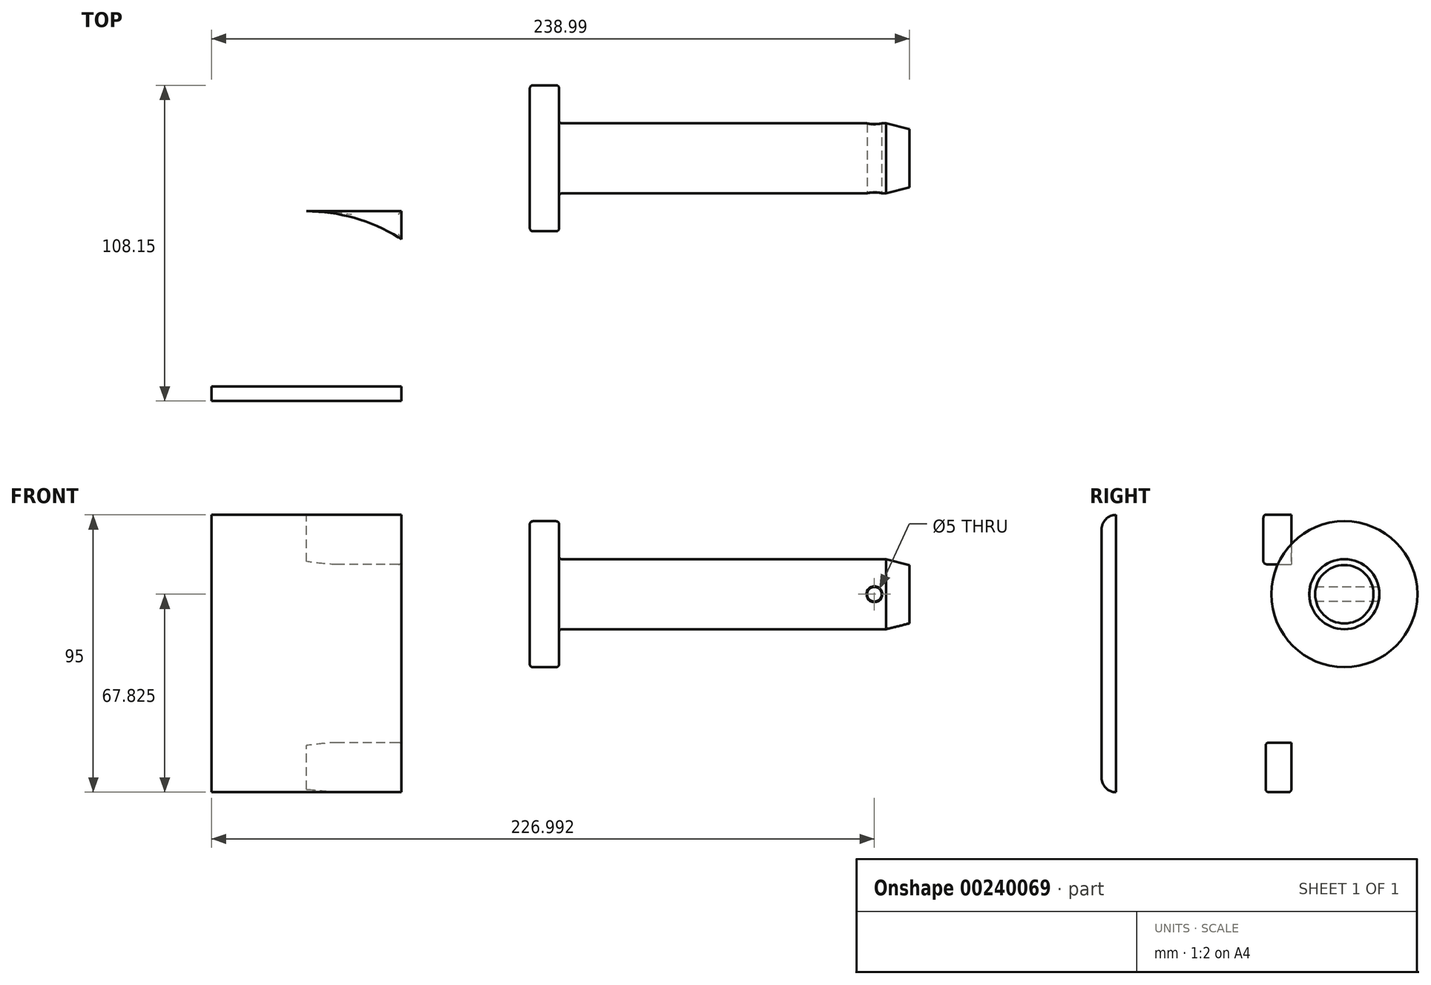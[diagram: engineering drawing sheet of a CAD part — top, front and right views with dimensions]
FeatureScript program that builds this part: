
annotation { "Feature Type Name" : "Feature", "Feature Type Description" : "" }
export const myFeature = defineFeature(function(context is Context, id is Id, definition is map)
    precondition{}
    {
        {
            var Q0;
            Q0=qCreatedBy(makeId("Right.planeOp"),FACE);
            var sketch = newSketch(context, id + "F0", { "sketchPlane" : qUnion([Q0])});
            skLineSegment(sketch, "E0", {"start": v(-83.15, 71.47) * mm, "end": v(-83.15, -13.53) * mm});
            skLineSegment(sketch, "E1", {"start": v(-78.15, 76.47) * mm, "end": v(-18.15, 76.47) * mm});
            skLineSegment(sketch, "E2", {"start": v(-78.15, -18.53) * mm, "end": v(-18.15, -18.53) * mm});
            skPoint(sketch, "E3.visualSharp", {"position": v(-83.15, 76.47) * mm});
            skArc(sketch, "E3.filletArc", {"start": v(-78.15, 76.47) * mm, "mid": v(-81.68, 75) * mm, "end": v(-83.15, 71.47) * mm});
            skPoint(sketch, "E4.visualSharp", {"position": v(-83.15, -18.53) * mm});
            skArc(sketch, "E4.filletArc", {"start": v(-83.15, -13.53) * mm, "mid": v(-81.68, -17.07) * mm, "end": v(-78.15, -18.53) * mm});
            skLineSegment(sketch, "E5.0", {"start": v(-65.15, 59.47) * mm, "end": v(-18.15, 59.47) * mm});
            skLineSegment(sketch, "E5.1", {"start": v(-66.15, 58.47) * mm, "end": v(-66.15, -0.53) * mm});
            skLineSegment(sketch, "E5.2", {"start": v(-65.15, -1.53) * mm, "end": v(-18.15, -1.53) * mm});
            skLineSegment(sketch, "E6", {"start": v(-18.15, 76.47) * mm, "end": v(-18.15, 59.47) * mm});
            skLineSegment(sketch, "E7", {"start": v(-18.15, -1.53) * mm, "end": v(-18.15, -18.53) * mm});
            skPoint(sketch, "E8.visualSharp", {"position": v(-66.15, 59.47) * mm});
            skArc(sketch, "E8.filletArc", {"start": v(-65.15, 59.47) * mm, "mid": v(-65.86, 59.17) * mm, "end": v(-66.15, 58.47) * mm});
            skPoint(sketch, "E9.visualSharp", {"position": v(-66.15, -1.53) * mm});
            skArc(sketch, "E9.filletArc", {"start": v(-66.15, -0.53) * mm, "mid": v(-65.86, -1.24) * mm, "end": v(-65.15, -1.53) * mm});
            skSolve(sketch);
        }
        {
            var Q0;
            Q0=makeQuery(id+"F0.imprint","IMPRINT",FACE,{"disambiguationData":[TD([[makeQuery(id+"F0.imprint","IMPRINT",EDGE,{"derivedFrom":sQuery(id+"F0.wireOp",EDGE,"E0")}),1.0]])]});
            extrude(context, id + "F1", {"entities" : qUnion([Q0]), "depth" : 65 * mm});
        }
        {
            var Q0;
            Q0=makeQuery(id+"F1.opExtrude","SWEPT_FACE",FACE,{"disambiguationData":[OSD([sQuery(id+"F0.wireOp",EDGE,"E1")])]});
            var sketch = newSketch(context, id + "F2", { "sketchPlane" : qUnion([Q0])});
            skCircle(sketch, "E10", {"center": v(32.5, -43.65) * mm, "radius": 12.5 * mm});
            skPoint(sketch, "E11", {"position": v(32.5, -18.15) * mm});
            skArc(sketch, "E12", {"start": v(32.5, -18.15) * mm, "mid": v(49.44, -20.59) * mm, "end": v(65, -27.71) * mm});
            skArc(sketch, "E13", {"start": v(32.5, -18.15) * mm, "mid": v(15.56, -20.59) * mm, "end": v(0, -27.71) * mm});
            skSolve(sketch);
        }
        {
            var Q0;
            Q0=makeQuery(id+"F2.imprint","IMPRINT",FACE,{"disambiguationData":[TD([[makeQuery(id+"F2.imprint","IMPRINT",EDGE,{"derivedFrom":sQuery(id+"F2.wireOp",EDGE,"E10")}),1.0]])]});
            extrude(context, id + "F3", {"entities" : qUnion([Q0]), "operationType" : NewBodyOperationType.REMOVE, "endBound" : BoundingType.THROUGH_ALL, "oppositeDirection" : true, "depth" : 25 * mm});
        }
        {
            var Q0;
            {var subQ0=sQuery(id+"F2.wireOp",EDGE,"E13");Q0=makeQuery(id+"F2.imprint","IMPRINT",FACE,{"disambiguationData":[TD([[makeQuery(id+"F2.imprint","IMPRINT",EDGE,{"derivedFrom":subQ0}),-1.0]])]});}
            extrude(context, id + "F4", {"entities" : qUnion([Q0]), "operationType" : NewBodyOperationType.REMOVE, "endBound" : BoundingType.THROUGH_ALL, "oppositeDirection" : true, "depth" : 25 * mm});
        }
        {
            var Q0;
            {var subQ0=sQuery(id+"F2.wireOp",EDGE,"E12");Q0=makeQuery(id+"F2.imprint","IMPRINT",FACE,{"disambiguationData":[TD([[makeQuery(id+"F2.imprint","IMPRINT",EDGE,{"derivedFrom":subQ0}),1.0]])]});}
            extrude(context, id + "F5", {"entities" : qUnion([Q0]), "operationType" : NewBodyOperationType.REMOVE, "endBound" : BoundingType.THROUGH_ALL, "oppositeDirection" : true, "depth" : 25 * mm});
        }
        {
            var Q0;
            Q0=qCreatedBy(makeId("Front.planeOp"),FACE);
            var sketch = newSketch(context, id + "F6", { "sketchPlane" : qUnion([Q0])});
            skLineSegment(sketch, "E14", {"start": v(239, 49.3) * mm, "end": v(109, 49.3) * mm});
            skLineSegment(sketch, "E15", {"start": v(239, 49.3) * mm, "end": v(239, 59.3) * mm});
            skLineSegment(sketch, "E16", {"start": v(109, 49.3) * mm, "end": v(109, 73.3) * mm});
            skLineSegment(sketch, "E17", {"start": v(110, 74.3) * mm, "end": v(118, 74.3) * mm});
            skLineSegment(sketch, "E18", {"start": v(119, 73.3) * mm, "end": v(119, 62.3) * mm});
            skLineSegment(sketch, "E19", {"start": v(120, 61.3) * mm, "end": v(231, 61.3) * mm});
            skLineSegment(sketch, "E20", {"start": v(239, 59.3) * mm, "end": v(231, 61.3) * mm});
            skPoint(sketch, "E21.orphan", {"position": v(239, 61.3) * mm});
            skPoint(sketch, "E22.visualSharp", {"position": v(119, 61.3) * mm});
            skArc(sketch, "E22.filletArc", {"start": v(119, 62.3) * mm, "mid": v(119.29, 61.59) * mm, "end": v(120, 61.3) * mm});
            skPoint(sketch, "E23.visualSharp", {"position": v(119, 74.3) * mm});
            skArc(sketch, "E23.filletArc", {"start": v(119, 73.3) * mm, "mid": v(118.7, 74) * mm, "end": v(118, 74.3) * mm});
            skPoint(sketch, "E24.visualSharp", {"position": v(109, 74.3) * mm});
            skArc(sketch, "E24.filletArc", {"start": v(110, 74.3) * mm, "mid": v(109.29, 74) * mm, "end": v(109, 73.3) * mm});
            skSolve(sketch);
        }
        {
            var Q0;
            Q0=makeQuery(id+"F6.imprint","IMPRINT",FACE,{"disambiguationData":[TD([[makeQuery(id+"F6.imprint","IMPRINT",EDGE,{"derivedFrom":sQuery(id+"F6.wireOp",EDGE,"E14")}),-1.0]])]});
            var Q1;
            Q1=sQuery(id+"F6.wireOp",EDGE,"E14");
            revolve(context, id + "F7", {"entities" : qUnion([Q0]), "axis" : qUnion([Q1]), "revolveType" : RevolveType.FULL});
        }
        {
            var Q0;
            Q0=qCreatedBy(makeId("Front.planeOp"),FACE);
            var sketch = newSketch(context, id + "F8", { "sketchPlane" : qUnion([Q0])});
            skCircle(sketch, "E25", {"center": v(227, 49.3) * mm, "radius": 2.5 * mm});
            skSolve(sketch);
        }
        {
            var Q0;
            Q0 = qSketchRegion(id + "F8", true);
            extrude(context, id + "F9", {"entities" : qUnion([Q0]), "operationType" : NewBodyOperationType.REMOVE, "endBound" : BoundingType.SYMMETRIC, "oppositeDirection" : true, "depth" : 50 * mm});
        }
        {
            var Q0;
            Q0=makeQuery(id+"F9.boolean.opBoolean","INTERSECT",EDGE,{"disambiguationData":[OD(1.0)],"derivedFrom":[makeQuery(id+"F7.opRevolve","SWEPT_FACE",FACE,{"disambiguationData":[OSD([sQuery(id+"F6.wireOp",EDGE,"E19")])]}),makeQuery(id+"F9.opExtrude","SWEPT_FACE",FACE,{"disambiguationData":[OSD([sQuery(id+"F8.wireOp",EDGE,"E25")])]})]});
            fillet(context, id + "F10", {"entities" : qUnion([Q0]), "radius" : .2 * mm, "tangentPropagation" : true, "allowEdgeOverflow" : false});
        }
        {
            var Q0;
            Q0=makeQuery(id+"F9.boolean.opBoolean","INTERSECT",EDGE,{"disambiguationData":[OD(0.0)],"derivedFrom":[makeQuery(id+"F7.opRevolve","SWEPT_FACE",FACE,{"disambiguationData":[OSD([sQuery(id+"F6.wireOp",EDGE,"E19")])]}),makeQuery(id+"F9.opExtrude","SWEPT_FACE",FACE,{"disambiguationData":[OSD([sQuery(id+"F8.wireOp",EDGE,"E25")])]})]});
            fillet(context, id + "F11", {"entities" : qUnion([Q0]), "radius" : .2 * mm, "tangentPropagation" : true, "allowEdgeOverflow" : false});
        }
        {
            var Q0;
            Q0=makeQuery(id+"F1.opExtrude","CAP_EDGE",EDGE,{"disambiguationData":[OSD([sQuery(id+"F0.wireOp",EDGE,"E1")])],"isStart":true});
            var Q1;
            Q1=makeQuery(id+"F5.boolean.opBoolean","MERGE",EDGE,{"derivedFrom":[makeQuery(id+"F4.boolean.opBoolean","COPY",EDGE,{"derivedFrom":makeQuery(id+"F4.opExtrude","CAP_EDGE",EDGE,{"disambiguationData":[OSD([sQuery(id+"F2.wireOp",EDGE,"E13")])],"isStart":true})}),makeQuery(id+"F5.opExtrude","CAP_EDGE",EDGE,{"disambiguationData":[OSD([sQuery(id+"F2.wireOp",EDGE,"E12")])],"isStart":true})]});
            var Q2;
            Q2=makeQuery(id+"F5.boolean.opBoolean","INTERSECT",EDGE,{"derivedFrom":[makeQuery(id+"F1.opExtrude","SWEPT_FACE",FACE,{"disambiguationData":[OSD([sQuery(id+"F0.wireOp",EDGE,"E5.0")])]}),makeQuery(id+"F5.opExtrude","SWEPT_FACE",FACE,{"disambiguationData":[OSD([sQuery(id+"F2.wireOp",EDGE,"E12")])]})]});
            var Q3;
            Q3=makeQuery(id+"F1.opExtrude","CAP_EDGE",EDGE,{"disambiguationData":[OSD([sQuery(id+"F0.wireOp",EDGE,"E5.0")])],"isStart":true});
            var Q4;
            Q4=makeQuery(id+"F1.opExtrude","CAP_EDGE",EDGE,{"disambiguationData":[OSD([sQuery(id+"F0.wireOp",EDGE,"E1")])],"isStart":false});
            var Q5;
            Q5=makeQuery(id+"F1.opExtrude","CAP_EDGE",EDGE,{"disambiguationData":[OSD([sQuery(id+"F0.wireOp",EDGE,"E5.2")])],"isStart":false});
            var Q6;
            Q6=makeQuery(id+"F1.opExtrude","CAP_EDGE",EDGE,{"disambiguationData":[OSD([sQuery(id+"F0.wireOp",EDGE,"E5.1")])],"isStart":false});
            var Q7;
            Q7=makeQuery(id+"F5.boolean.opBoolean","INTERSECT",EDGE,{"derivedFrom":[makeQuery(id+"F1.opExtrude","SWEPT_FACE",FACE,{"disambiguationData":[OSD([sQuery(id+"F0.wireOp",EDGE,"E5.2")])]}),makeQuery(id+"F5.opExtrude","SWEPT_FACE",FACE,{"disambiguationData":[OSD([sQuery(id+"F2.wireOp",EDGE,"E12")])]})]});
            var Q8;
            {var subQ9=sQuery(id+"F0.wireOp",EDGE,"E2");var subQ10=sQuery(id+"F0.wireOp",EDGE,"E1");var subQ12=makeQuery(id+"F1.opExtrude","SWEPT_FACE",FACE,{"disambiguationData":[OSD([subQ9])]});var subQ14=sQuery(id+"F2.wireOp",EDGE,"E12");Q8=makeQuery(id+"F5.boolean.opBoolean","COPY",EDGE,{"disambiguationData":[TD([subQ12])],"derivedFrom":makeQuery(id+"F5.opExtrude","SWEPT_EDGE",EDGE,{"disambiguationData":[OSD([subQ10,subQ14])]})});}
            var Q9;
            {var subQ10=sQuery(id+"F0.wireOp",EDGE,"E1");var subQ12=makeQuery(id+"F1.opExtrude","SWEPT_FACE",FACE,{"disambiguationData":[OSD([subQ10])]});var subQ14=sQuery(id+"F2.wireOp",EDGE,"E12");Q9=makeQuery(id+"F5.boolean.opBoolean","COPY",EDGE,{"disambiguationData":[TD([subQ12])],"derivedFrom":makeQuery(id+"F5.opExtrude","SWEPT_EDGE",EDGE,{"disambiguationData":[OSD([subQ10,subQ14])]})});}
            var Q10;
            Q10=makeQuery(id+"F5.boolean.opBoolean","INTERSECT",EDGE,{"derivedFrom":[makeQuery(id+"F1.opExtrude","SWEPT_FACE",FACE,{"disambiguationData":[OSD([sQuery(id+"F0.wireOp",EDGE,"E2")])]}),makeQuery(id+"F5.opExtrude","SWEPT_FACE",FACE,{"disambiguationData":[OSD([sQuery(id+"F2.wireOp",EDGE,"E12")])]})]});
            var Q11;
            {var subQ1=sQuery(id+"F0.wireOp",EDGE,"E2");var subQ2=sQuery(id+"F0.wireOp",EDGE,"E1");var subQ3=sQuery(id+"F2.wireOp",EDGE,"E13");Q11=makeQuery(id+"F4.boolean.opBoolean","COPY",EDGE,{"disambiguationData":[TD([makeQuery(id+"F1.opExtrude","SWEPT_FACE",FACE,{"disambiguationData":[OSD([subQ1])]})])],"derivedFrom":makeQuery(id+"F4.opExtrude","SWEPT_EDGE",EDGE,{"disambiguationData":[OSD([subQ2,subQ3])]})});}
            var Q12;
            {var subQ1=sQuery(id+"F0.wireOp",EDGE,"E1");var subQ2=sQuery(id+"F2.wireOp",EDGE,"E13");Q12=makeQuery(id+"F4.boolean.opBoolean","COPY",EDGE,{"disambiguationData":[TD([makeQuery(id+"F1.opExtrude","SWEPT_FACE",FACE,{"disambiguationData":[OSD([subQ1])]})])],"derivedFrom":makeQuery(id+"F4.opExtrude","SWEPT_EDGE",EDGE,{"disambiguationData":[OSD([subQ1,subQ2])]})});}
            var Q13;
            Q13=makeQuery(id+"F1.opExtrude","CAP_EDGE",EDGE,{"disambiguationData":[OSD([sQuery(id+"F0.wireOp",EDGE,"E5.0")])],"isStart":false});
            var Q14;
            Q14=makeQuery(id+"F1.opExtrude","SWEPT_FACE",FACE,{"disambiguationData":[OSD([sQuery(id+"F0.wireOp",EDGE,"E2")])]});
            var Q15;
            Q15=makeQuery(id+"F1.opExtrude","CAP_EDGE",EDGE,{"disambiguationData":[OSD([sQuery(id+"F0.wireOp",EDGE,"E5.2")])],"isStart":true});
            var Q16;
            Q16=makeQuery(id+"F1.opExtrude","CAP_EDGE",EDGE,{"disambiguationData":[OSD([sQuery(id+"F0.wireOp",EDGE,"E5.1")])],"isStart":true});
            fillet(context, id + "F12", {"entities" : qUnion([Q0, Q1, Q2, Q3, Q4, Q5, Q6, Q7, Q8, Q9, Q10, Q11, Q12, Q13, Q14, Q15, Q16]), "radius" : 1 * mm, "tangentPropagation" : true, "allowEdgeOverflow" : false});
        }
    });
